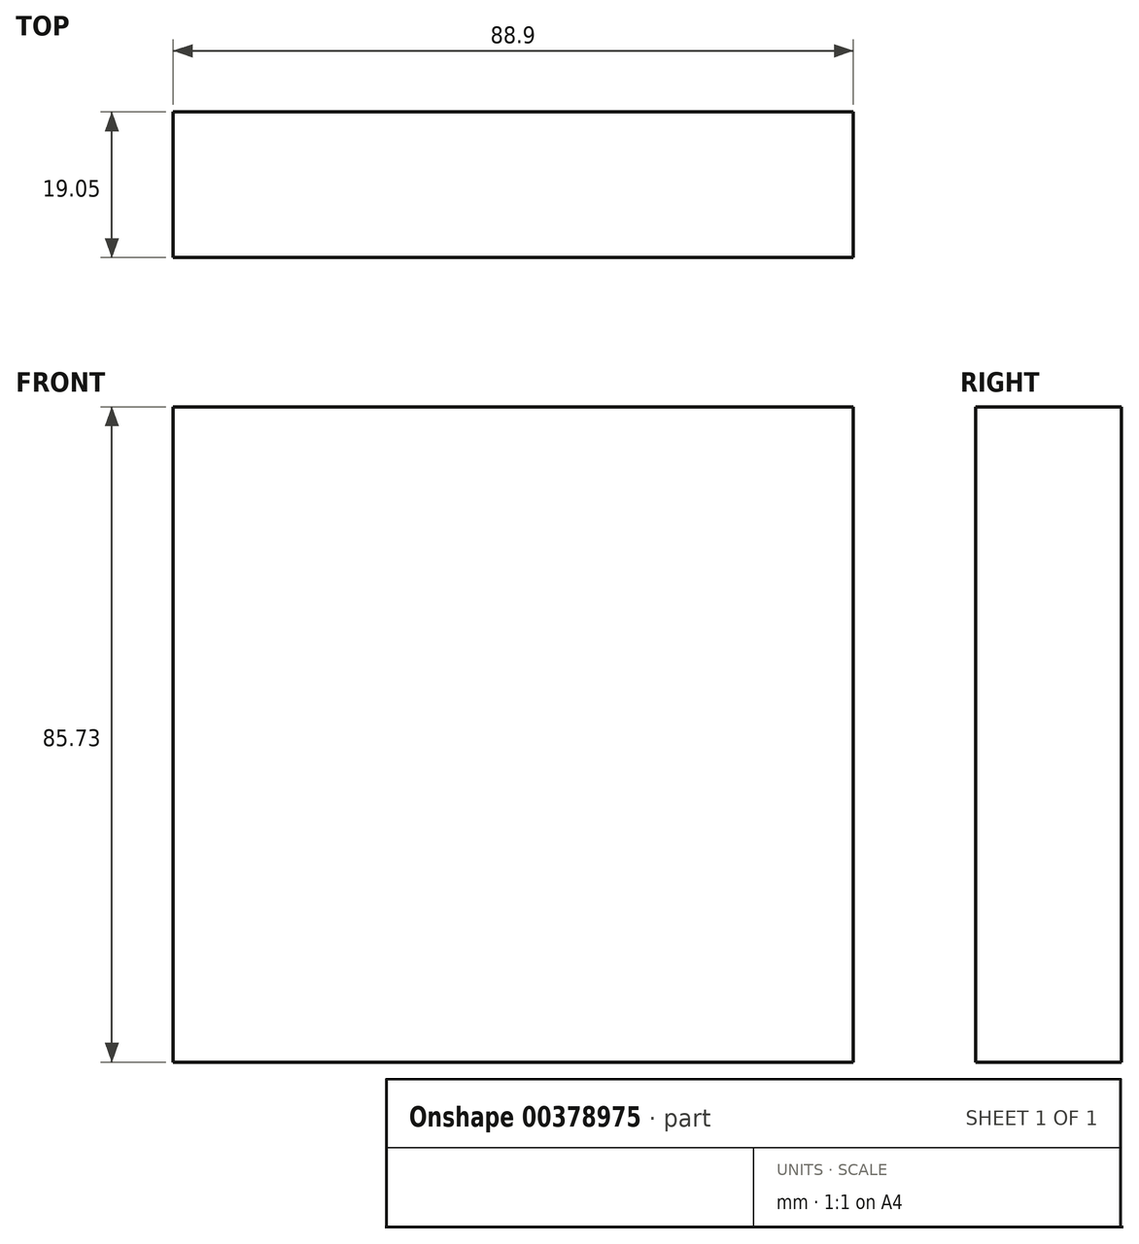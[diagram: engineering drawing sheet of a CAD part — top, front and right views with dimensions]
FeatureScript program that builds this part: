
annotation { "Feature Type Name" : "Feature", "Feature Type Description" : "" }
export const myFeature = defineFeature(function(context is Context, id is Id, definition is map)
    precondition{}
    {
        {
            var Q0;
            Q0=qCreatedBy(makeId("Front.planeOp"),FACE);
            var sketch = newSketch(context, id + "F0", { "sketchPlane" : qUnion([Q0])});
            skLineSegment(sketch, "E0.bottom", {"start": v(-88.9, 44.8) * mm, "end": v(0, 44.8) * mm});
            skLineSegment(sketch, "E0.top", {"start": v(-88.9, -40.93) * mm, "end": v(0, -40.93) * mm});
            skLineSegment(sketch, "E0.left", {"start": v(-88.9, 44.8) * mm, "end": v(-88.9, -40.93) * mm});
            skLineSegment(sketch, "E0.right", {"start": v(0, 44.8) * mm, "end": v(0, -40.93) * mm});
            skSolve(sketch);
        }
        {
            var Q0;
            Q0 = qSketchRegion(id + "F0", true);
            extrude(context, id + "F1", {"entities" : qUnion([Q0]), "depth" : 19.05 * mm, "offsetDistance" : 25.4 * mm});
        }
    });
